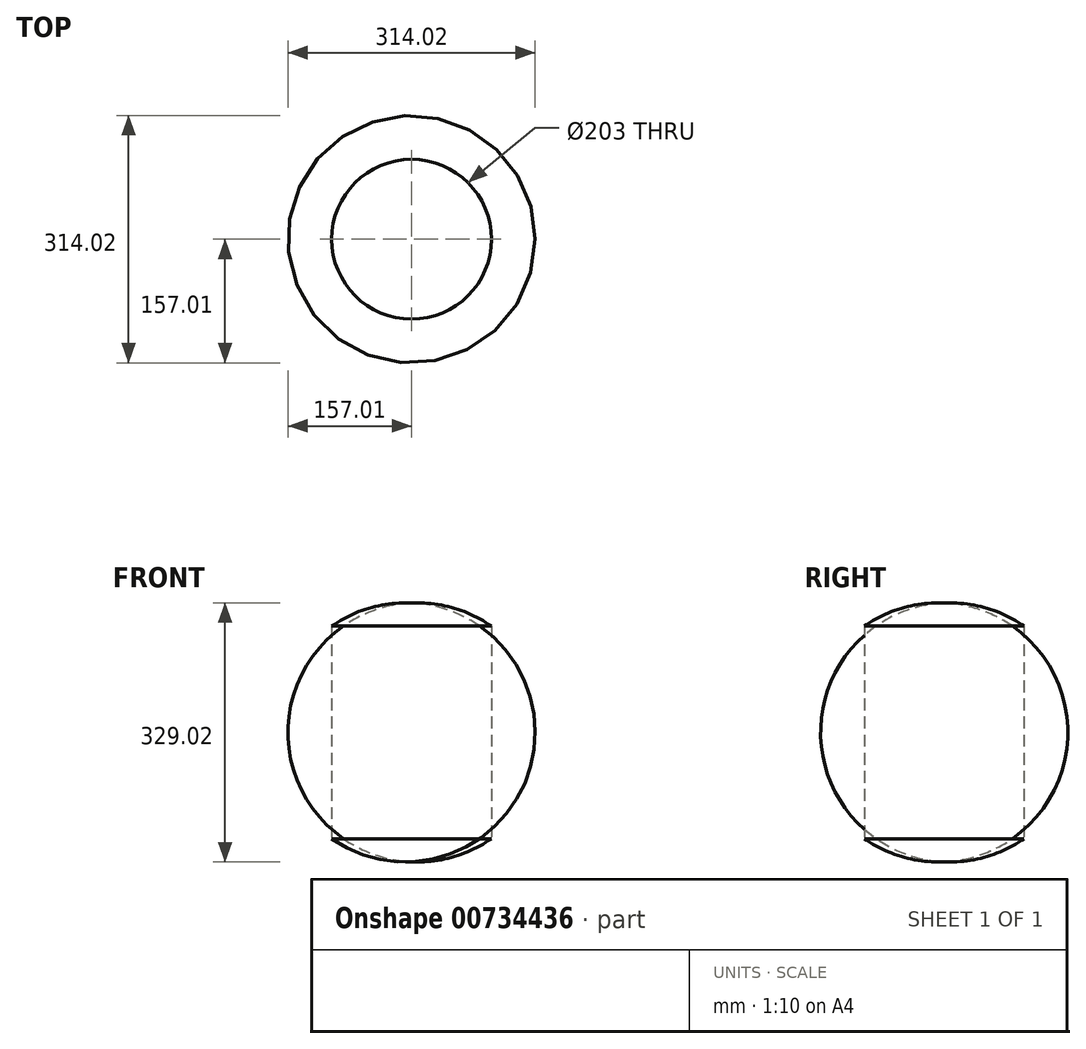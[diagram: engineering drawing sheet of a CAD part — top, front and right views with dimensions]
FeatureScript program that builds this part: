
annotation { "Feature Type Name" : "Feature", "Feature Type Description" : "" }
export const myFeature = defineFeature(function(context is Context, id is Id, definition is map)
    precondition{}
    {
        {
            var Q0;
            Q0=qCreatedBy(makeId("Right.planeOp"),FACE);
            var sketch = newSketch(context, id + "F0", { "sketchPlane" : qUnion([Q0])});
            skLineSegment(sketch, "E0", {"start": v(0, 270) * mm, "end": v(0, 0) * mm});
            skPoint(sketch, "E1.endSnap0", {"position": v(0, 135) * mm});
            skArc(sketch, "E2", {"start": v(0, 270) * mm, "mid": v(-70.5, 135) * mm, "end": v(0, 0) * mm});
            skPoint(sketch, "E1.end.orphan", {"position": v(-70.5, 135) * mm});
            skPoint(sketch, "E1.start.orphan", {"position": v(0, 135) * mm});
            skLineSegment(sketch, "E3", {"start": v(101.5, 0) * mm, "end": v(101.5, 321.32) * mm});
            skSolve(sketch);
        }
        {
            var Q0;
            Q0=makeQuery(id+"F0.imprint","IMPRINT",FACE,{"disambiguationData":[TD([[makeQuery(id+"F0.imprint","IMPRINT",EDGE,{"derivedFrom":sQuery(id+"F0.wireOp",EDGE,"E0")}),-1.0]])]});
            var Q1;
            Q1=sQuery(id+"F0.wireOp",EDGE,"E3");
            revolve(context, id + "F1", {"surfaceOperationType" : NewSurfaceOperationType.NEW, "entities" : qUnion([Q0]), "axis" : qUnion([Q1]), "revolveType" : RevolveType.FULL});
        }
    });
